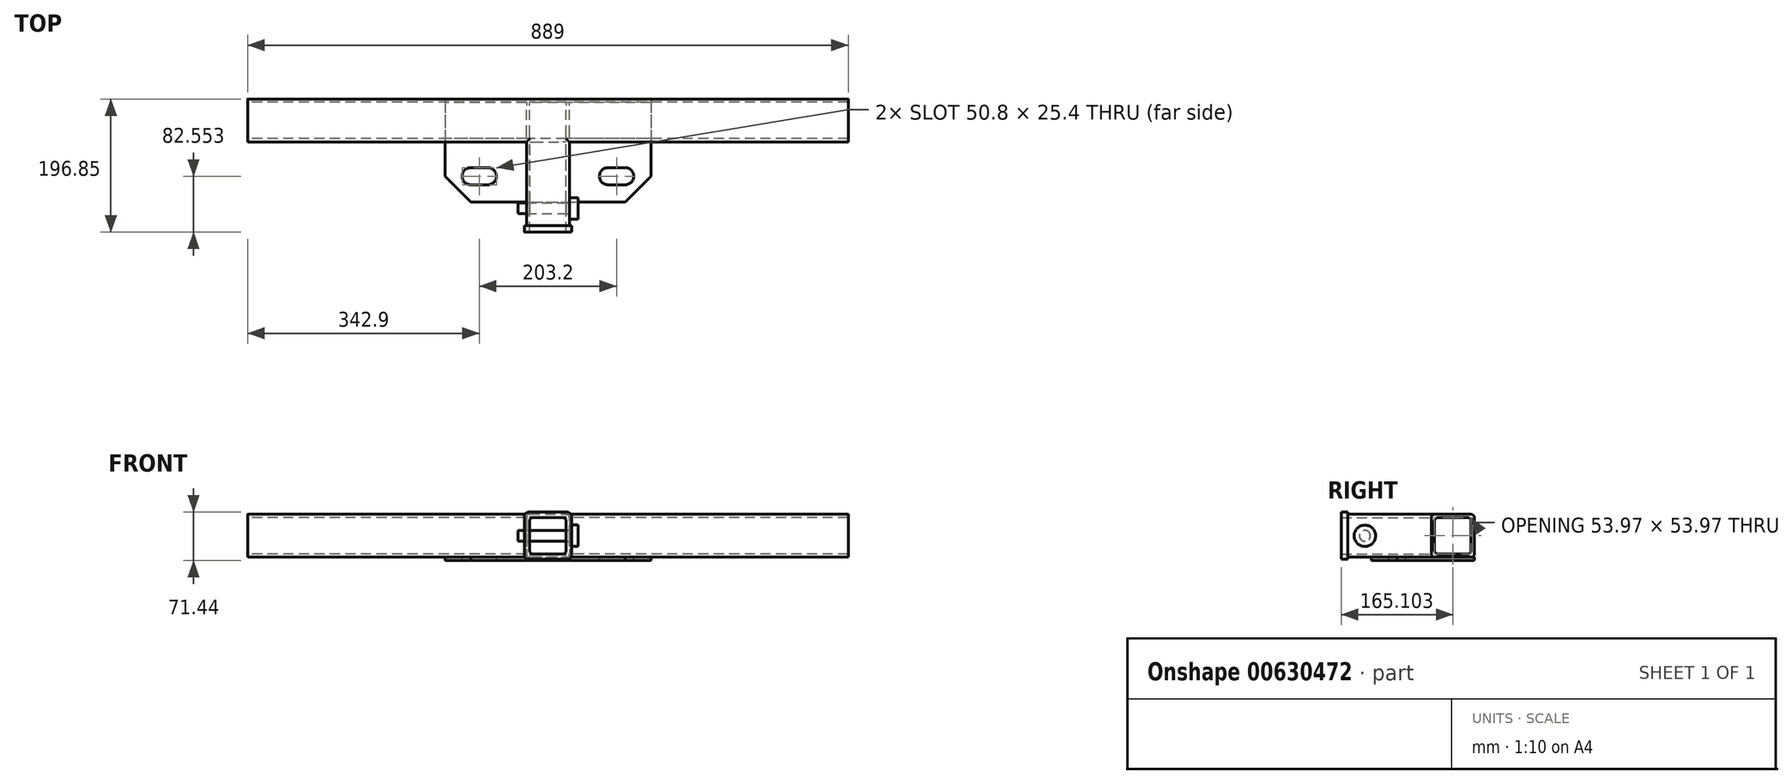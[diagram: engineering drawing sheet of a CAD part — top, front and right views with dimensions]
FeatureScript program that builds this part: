
annotation { "Feature Type Name" : "Feature", "Feature Type Description" : "" }
export const myFeature = defineFeature(function(context is Context, id is Id, definition is map)
    precondition{}
    {
        {
            var Q0;
            Q0=qCreatedBy(makeId("Right.planeOp"),FACE);
            var sketch = newSketch(context, id + "F0", { "sketchPlane" : qUnion([Q0])});
            skLineSegment(sketch, "E0.0", {"start": v(-90.49, 0) * mm, "end": v(-26.99, 0) * mm});
            skLineSegment(sketch, "E0.1", {"start": v(-90.49, 0) * mm, "end": v(-90.49, -63.5) * mm});
            skLineSegment(sketch, "E0.2", {"start": v(-90.49, -63.5) * mm, "end": v(-26.99, -63.5) * mm});
            skLineSegment(sketch, "E0.3", {"start": v(-26.99, 0) * mm, "end": v(-26.99, -63.5) * mm});
            skLineSegment(sketch, "E1.0", {"start": v(-31.75, -4.76) * mm, "end": v(-31.75, -58.74) * mm});
            skLineSegment(sketch, "E1.1", {"start": v(-85.73, -4.76) * mm, "end": v(-31.75, -4.76) * mm});
            skLineSegment(sketch, "E1.2", {"start": v(-85.73, -4.76) * mm, "end": v(-85.73, -58.74) * mm});
            skLineSegment(sketch, "E1.3", {"start": v(-85.73, -58.74) * mm, "end": v(-31.75, -58.74) * mm});
            skSolve(sketch);
        }
        {
            var Q0;
            Q0=makeQuery(id+"F0.imprint","IMPRINT",FACE,{"disambiguationData":[TD([[makeQuery(id+"F0.imprint","IMPRINT",EDGE,{"derivedFrom":sQuery(id+"F0.wireOp",EDGE,"E0.0")}),-1.0]])]});
            var Q1;
            Q1=qConstructionFilter(qBodyType(qCreatedBy(id+"F0",EDGE),BodyType.WIRE),ConstructionObject.NO);
            extrude(context, id + "F1", {"entities" : qUnion([Q0]), "surfaceEntities" : qUnion([Q1]), "depth" : 889 * mm, "symmetric" : true});
        }
        {
            var Q0;
            Q0=makeQuery(id+"F1.opExtrude","SWEPT_FACE",FACE,{"disambiguationData":[OSD([sQuery(id+"F0.wireOp",EDGE,"E0.1")])]});
            var sketch = newSketch(context, id + "F2", { "sketchPlane" : qUnion([Q0])});
            skLineSegment(sketch, "E2.bottom", {"start": v(-31.75, 0) * mm, "end": v(31.75, 0) * mm});
            skLineSegment(sketch, "E2.top", {"start": v(-31.75, -63.5) * mm, "end": v(31.75, -63.5) * mm});
            skLineSegment(sketch, "E2.left", {"start": v(-31.75, 0) * mm, "end": v(-31.75, -63.5) * mm});
            skLineSegment(sketch, "E2.right", {"start": v(31.75, 0) * mm, "end": v(31.75, -63.5) * mm});
            skLineSegment(sketch, "E3.0", {"start": v(-26.99, -4.76) * mm, "end": v(-26.99, -58.74) * mm});
            skLineSegment(sketch, "E3.1", {"start": v(-26.99, -4.76) * mm, "end": v(26.99, -4.76) * mm});
            skLineSegment(sketch, "E3.2", {"start": v(26.99, -4.76) * mm, "end": v(26.99, -58.74) * mm});
            skLineSegment(sketch, "E3.3", {"start": v(-26.99, -58.74) * mm, "end": v(26.99, -58.74) * mm});
            skLineSegment(sketch, "E4", {"start": v(0, 0) * mm, "end": v(0, 11.04) * mm, "construction": true});
            skSolve(sketch);
        }
        {
            var Q0;
            Q0=qSketchRegion(id+"F2",true);
            var Q1;
            Q1=makeQuery(id+"F1.opExtrude","SWEPT_BODY",BODY,{"disambiguationData":[OSD([sQuery(id+"F0.wireOp",EDGE,"E0.0"),sQuery(id+"F0.wireOp",EDGE,"E0.1"),sQuery(id+"F0.wireOp",EDGE,"E0.2"),sQuery(id+"F0.wireOp",EDGE,"E0.3"),sQuery(id+"F0.wireOp",EDGE,"E1.0"),sQuery(id+"F0.wireOp",EDGE,"E1.1"),sQuery(id+"F0.wireOp",EDGE,"E1.2"),sQuery(id+"F0.wireOp",EDGE,"E1.3")])]});
            extrude(context, id + "F3", {"entities" : qUnion([Q0]), "operationType" : NewBodyOperationType.ADD, "depth" : 127 * mm, "hasSecondDirection" : true, "secondDirectionBound" : BoundingType.UP_TO_BODY, "secondDirectionOppositeDirection" : true, "secondDirectionBoundEntityBody" : qUnion([Q1]), "secondDirectionDepth" : 25.4 * mm});
        }
        {
            var Q0;
            Q0=makeQuery(id+"F1.opExtrude","SWEPT_EDGE",EDGE,{"disambiguationData":[OSD([sQuery(id+"F0.wireOp",EDGE,"E0.0"),sQuery(id+"F0.wireOp",EDGE,"E0.1")])]});
            var Q1;
            Q1=makeQuery(id+"F1.opExtrude","SWEPT_EDGE",EDGE,{"disambiguationData":[OSD([sQuery(id+"F0.wireOp",EDGE,"E0.0"),sQuery(id+"F0.wireOp",EDGE,"E0.3")])]});
            var Q2;
            Q2=makeQuery(id+"F1.opExtrude","SWEPT_EDGE",EDGE,{"disambiguationData":[OSD([sQuery(id+"F0.wireOp",EDGE,"E0.2"),sQuery(id+"F0.wireOp",EDGE,"E0.3")])]});
            var Q3;
            Q3=makeQuery(id+"F1.opExtrude","SWEPT_EDGE",EDGE,{"disambiguationData":[OSD([sQuery(id+"F0.wireOp",EDGE,"E0.1"),sQuery(id+"F0.wireOp",EDGE,"E0.2")])]});
            var Q4;
            Q4=makeQuery(id+"F1.opExtrude","SWEPT_EDGE",EDGE,{"disambiguationData":[OSD([sQuery(id+"F0.wireOp",EDGE,"E1.0"),sQuery(id+"F0.wireOp",EDGE,"E1.1")])]});
            var Q5;
            Q5=makeQuery(id+"F1.opExtrude","SWEPT_EDGE",EDGE,{"disambiguationData":[OSD([sQuery(id+"F0.wireOp",EDGE,"E1.1"),sQuery(id+"F0.wireOp",EDGE,"E1.2")])]});
            var Q6;
            Q6=makeQuery(id+"F1.opExtrude","SWEPT_EDGE",EDGE,{"disambiguationData":[OSD([sQuery(id+"F0.wireOp",EDGE,"E1.0"),sQuery(id+"F0.wireOp",EDGE,"E1.3")])]});
            var Q7;
            Q7=makeQuery(id+"F1.opExtrude","SWEPT_EDGE",EDGE,{"disambiguationData":[OSD([sQuery(id+"F0.wireOp",EDGE,"E1.2"),sQuery(id+"F0.wireOp",EDGE,"E1.3")])]});
            var Q8;
            Q8=makeQuery(id+"F3.opExtrude","SWEPT_EDGE",EDGE,{"disambiguationData":[OSD([sQuery(id+"F0.wireOp",EDGE,"E0.0"),sQuery(id+"F0.wireOp",EDGE,"E0.1"),sQuery(id+"F2.wireOp",EDGE,"E2.bottom"),sQuery(id+"F2.wireOp",EDGE,"E2.left")])]});
            var Q9;
            Q9=makeQuery(id+"F3.opExtrude","SWEPT_EDGE",EDGE,{"disambiguationData":[OSD([sQuery(id+"F0.wireOp",EDGE,"E0.0"),sQuery(id+"F0.wireOp",EDGE,"E0.1"),sQuery(id+"F2.wireOp",EDGE,"E2.bottom"),sQuery(id+"F2.wireOp",EDGE,"E2.right")])]});
            var Q10;
            Q10=makeQuery(id+"F3.opExtrude","SWEPT_EDGE",EDGE,{"disambiguationData":[OSD([sQuery(id+"F0.wireOp",EDGE,"E0.1"),sQuery(id+"F0.wireOp",EDGE,"E0.2"),sQuery(id+"F2.wireOp",EDGE,"E2.top"),sQuery(id+"F2.wireOp",EDGE,"E2.right")])]});
            var Q11;
            Q11=makeQuery(id+"F3.opExtrude","SWEPT_EDGE",EDGE,{"disambiguationData":[OSD([sQuery(id+"F0.wireOp",EDGE,"E0.1"),sQuery(id+"F0.wireOp",EDGE,"E0.2"),sQuery(id+"F2.wireOp",EDGE,"E2.top"),sQuery(id+"F2.wireOp",EDGE,"E2.left")])]});
            var Q12;
            {var subQ0=sQuery(id+"F2.wireOp",EDGE,"E3.1");var subQ1=sQuery(id+"F2.wireOp",EDGE,"E3.0");Q12=makeQuery(id+"F3.boolean.opBoolean","SPLIT",EDGE,{"disambiguationData":[TD([makeQuery(id+"F1.opExtrude","SWEPT_FACE",FACE,{"disambiguationData":[OSD([sQuery(id+"F0.wireOp",EDGE,"E0.1")])]})])],"derivedFrom":makeQuery(id+"F3.opExtrude","SWEPT_EDGE",EDGE,{"disambiguationData":[OSD([subQ1,subQ0])]})});}
            var Q13;
            {var subQ0=sQuery(id+"F2.wireOp",EDGE,"E3.2");var subQ1=sQuery(id+"F2.wireOp",EDGE,"E3.1");Q13=makeQuery(id+"F3.boolean.opBoolean","SPLIT",EDGE,{"disambiguationData":[TD([makeQuery(id+"F1.opExtrude","SWEPT_FACE",FACE,{"disambiguationData":[OSD([sQuery(id+"F0.wireOp",EDGE,"E0.1")])]})])],"derivedFrom":makeQuery(id+"F3.opExtrude","SWEPT_EDGE",EDGE,{"disambiguationData":[OSD([subQ1,subQ0])]})});}
            var Q14;
            {var subQ0=sQuery(id+"F2.wireOp",EDGE,"E3.3");var subQ1=sQuery(id+"F2.wireOp",EDGE,"E3.0");Q14=makeQuery(id+"F3.boolean.opBoolean","SPLIT",EDGE,{"disambiguationData":[TD([makeQuery(id+"F1.opExtrude","SWEPT_FACE",FACE,{"disambiguationData":[OSD([sQuery(id+"F0.wireOp",EDGE,"E0.1")])]})])],"derivedFrom":makeQuery(id+"F3.opExtrude","SWEPT_EDGE",EDGE,{"disambiguationData":[OSD([subQ1,subQ0])]})});}
            var Q15;
            {var subQ0=sQuery(id+"F2.wireOp",EDGE,"E3.3");var subQ1=sQuery(id+"F2.wireOp",EDGE,"E3.2");Q15=makeQuery(id+"F3.boolean.opBoolean","SPLIT",EDGE,{"disambiguationData":[TD([makeQuery(id+"F1.opExtrude","SWEPT_FACE",FACE,{"disambiguationData":[OSD([sQuery(id+"F0.wireOp",EDGE,"E0.1")])]})])],"derivedFrom":makeQuery(id+"F3.opExtrude","SWEPT_EDGE",EDGE,{"disambiguationData":[OSD([subQ1,subQ0])]})});}
            fillet(context, id + "F4", {"entities" : qUnion([Q0, Q1, Q2, Q3, Q4, Q5, Q6, Q7, Q8, Q9, Q10, Q11, Q12, Q13, Q14, Q15]), "radius" : 5.08 * mm, "tangentPropagation" : true, "allowEdgeOverflow" : false});
        }
        {
            var Q0;
            Q0=makeQuery(id+"F3.boolean.opBoolean","MERGE",FACE,{"derivedFrom":[makeQuery(id+"F1.opExtrude","SWEPT_FACE",FACE,{"disambiguationData":[OSD([sQuery(id+"F0.wireOp",EDGE,"E0.0")])]}),makeQuery(id+"F3.opExtrude","SWEPT_FACE",FACE,{"disambiguationData":[OSD([sQuery(id+"F2.wireOp",EDGE,"E2.bottom")])]})]});
            var sketch = newSketch(context, id + "F5", { "sketchPlane" : qUnion([Q0])});
            skLineSegment(sketch, "E5.0", {"start": v(-444.5, -26.99) * mm, "end": v(444.5, -26.99) * mm});
            skLineSegment(sketch, "E6", {"start": v(0, -3.11) * mm, "end": v(0, -26.99) * mm, "construction": true});
            skLineSegment(sketch, "E7.0", {"start": v(-31.75, -90.49) * mm, "end": v(-444.5, -90.49) * mm});
            skLineSegment(sketch, "E8.0", {"start": v(444.5, -90.49) * mm, "end": v(31.75, -90.49) * mm});
            skLineSegment(sketch, "E9", {"start": v(-101.6, -26.99) * mm, "end": v(-101.6, -90.49) * mm});
            skLineSegment(sketch, "E10.0", {"start": v(-31.75, -217.49) * mm, "end": v(-31.75, -90.49) * mm});
            skLineSegment(sketch, "E10.1", {"start": v(31.75, -90.49) * mm, "end": v(31.75, -217.49) * mm});
            skLineSegment(sketch, "E11", {"start": v(-101.6, -90.49) * mm, "end": v(-31.75, -160.34) * mm});
            skLineSegment(sketch, "E12", {"start": v(-31.75, -160.34) * mm, "end": v(31.75, -160.34) * mm});
            skLineSegment(sketch, "E13", {"start": v(31.75, -160.34) * mm, "end": v(101.6, -90.49) * mm});
            skLineSegment(sketch, "E14", {"start": v(101.6, -90.49) * mm, "end": v(101.6, -26.99) * mm});
            skSolve(sketch);
        }
        {
            var Q0;
            Q0=makeQuery(id+"F3.boolean.opBoolean","MERGE",FACE,{"derivedFrom":[makeQuery(id+"F1.opExtrude","SWEPT_FACE",FACE,{"disambiguationData":[OSD([sQuery(id+"F0.wireOp",EDGE,"E0.2")])]}),makeQuery(id+"F3.opExtrude","SWEPT_FACE",FACE,{"disambiguationData":[OSD([sQuery(id+"F2.wireOp",EDGE,"E2.top")])]})]});
            var sketch = newSketch(context, id + "F6", { "sketchPlane" : qUnion([Q0])});
            skLineSegment(sketch, "E15.0", {"start": v(444.5, 26.99) * mm, "end": v(-444.5, 26.99) * mm});
            skLineSegment(sketch, "E16.bottom", {"start": v(-152.4, 26.99) * mm, "end": v(152.4, 26.99) * mm});
            skLineSegment(sketch, "E16.top", {"start": v(-114.3, 179.39) * mm, "end": v(114.3, 179.39) * mm});
            skLineSegment(sketch, "E16.right", {"start": v(152.4, 26.99) * mm, "end": v(152.4, 141.29) * mm});
            skLineSegment(sketch, "E17", {"start": v(0, 0) * mm, "end": v(0, 26.99) * mm, "construction": true});
            skLineSegment(sketch, "E18", {"start": v(-152.4, 141.29) * mm, "end": v(-114.3, 179.39) * mm});
            skLineSegment(sketch, "E19", {"start": v(-114.3, 179.39) * mm, "end": v(-152.4, 141.29) * mm});
            skLineSegment(sketch, "E20", {"start": v(152.4, 141.29) * mm, "end": v(114.3, 179.39) * mm});
            skLineSegment(sketch, "E21", {"start": v(-152.4, 26.99) * mm, "end": v(-152.4, 141.29) * mm});
            skLineSegment(sketch, "E22.bottom", {"start": v(-114.3, 153.99) * mm, "end": v(-88.9, 153.99) * mm});
            skLineSegment(sketch, "E22.top", {"start": v(-114.3, 128.59) * mm, "end": v(-88.9, 128.59) * mm});
            skLineSegment(sketch, "E22.left", {"start": v(-127, 141.29) * mm, "end": v(-127, 141.29) * mm});
            skLineSegment(sketch, "E22.right", {"start": v(-76.2, 141.29) * mm, "end": v(-76.2, 141.29) * mm});
            skPoint(sketch, "E23.visualSharp", {"position": v(-127, 153.99) * mm});
            skArc(sketch, "E23.filletArc", {"start": v(-114.3, 153.99) * mm, "mid": v(-123.28, 150.27) * mm, "end": v(-127, 141.29) * mm});
            skPoint(sketch, "E24.visualSharp", {"position": v(-76.2, 153.99) * mm});
            skArc(sketch, "E24.filletArc", {"start": v(-76.2, 141.29) * mm, "mid": v(-79.92, 150.27) * mm, "end": v(-88.9, 153.99) * mm});
            skPoint(sketch, "E25.visualSharp", {"position": v(-76.2, 128.59) * mm});
            skArc(sketch, "E25.filletArc", {"start": v(-88.9, 128.59) * mm, "mid": v(-79.92, 132.3) * mm, "end": v(-76.2, 141.29) * mm});
            skPoint(sketch, "E26.visualSharp", {"position": v(-127, 128.59) * mm});
            skArc(sketch, "E26.filletArc", {"start": v(-127, 141.29) * mm, "mid": v(-123.28, 132.3) * mm, "end": v(-114.3, 128.59) * mm});
            skArc(sketch, "E27.MirrorCS", {"start": v(88.9, 128.59) * mm, "mid": v(79.92, 132.3) * mm, "end": v(76.2, 141.29) * mm});
            skArc(sketch, "E28.MirrorCS", {"start": v(76.2, 141.29) * mm, "mid": v(79.92, 150.27) * mm, "end": v(88.9, 153.99) * mm});
            skArc(sketch, "E29.MirrorCS", {"start": v(127, 141.29) * mm, "mid": v(123.28, 132.3) * mm, "end": v(114.3, 128.59) * mm});
            skArc(sketch, "E30.MirrorCS", {"start": v(114.3, 153.99) * mm, "mid": v(123.28, 150.27) * mm, "end": v(127, 141.29) * mm});
            skLineSegment(sketch, "E31.MirrorCS", {"start": v(127, 141.29) * mm, "end": v(127, 141.29) * mm});
            skLineSegment(sketch, "E32.MirrorCS", {"start": v(76.2, 141.29) * mm, "end": v(76.2, 141.29) * mm});
            skPoint(sketch, "E33.MirrorP", {"position": v(76.2, 153.99) * mm});
            skPoint(sketch, "E34.MirrorP", {"position": v(76.2, 128.59) * mm});
            skLineSegment(sketch, "E35.MirrorCS", {"start": v(114.3, 153.99) * mm, "end": v(88.9, 153.99) * mm});
            skLineSegment(sketch, "E36.MirrorCS", {"start": v(114.3, 128.59) * mm, "end": v(88.9, 128.59) * mm});
            skPoint(sketch, "E37.MirrorP", {"position": v(127, 128.59) * mm});
            skPoint(sketch, "E38.MirrorP", {"position": v(127, 153.99) * mm});
            skSolve(sketch);
        }
        {
            var Q0;
            Q0=qSketchRegion(id+"F6",true);
            extrude(context, id + "F7", {"entities" : qUnion([Q0]), "operationType" : NewBodyOperationType.ADD, "depth" : 4.76 * mm});
        }
        {
            var Q0;
            Q0=makeQuery(id+"F3.opExtrude","CAP_FACE",FACE,{"disambiguationData":[OSD([sQuery(id+"F2.wireOp",EDGE,"E2.bottom"),sQuery(id+"F2.wireOp",EDGE,"E2.top"),sQuery(id+"F2.wireOp",EDGE,"E2.left"),sQuery(id+"F2.wireOp",EDGE,"E2.right"),sQuery(id+"F2.wireOp",EDGE,"E3.0"),sQuery(id+"F2.wireOp",EDGE,"E3.1"),sQuery(id+"F2.wireOp",EDGE,"E3.2"),sQuery(id+"F2.wireOp",EDGE,"E3.3")])],"isStart":false});
            var sketch = newSketch(context, id + "F8", { "sketchPlane" : qUnion([Q0])});
            skLineSegment(sketch, "E39.0", {"start": v(-21.9, -4.76) * mm, "end": v(21.9, -4.76) * mm});
            skArc(sketch, "E39.1", {"start": v(-26.99, -9.84) * mm, "mid": v(-25.5, -6.25) * mm, "end": v(-21.9, -4.76) * mm});
            skLineSegment(sketch, "E39.2", {"start": v(-26.99, -9.84) * mm, "end": v(-26.99, -53.66) * mm});
            skArc(sketch, "E39.3", {"start": v(-21.9, -58.74) * mm, "mid": v(-25.5, -57.25) * mm, "end": v(-26.99, -53.66) * mm});
            skLineSegment(sketch, "E39.4", {"start": v(-21.9, -58.74) * mm, "end": v(21.9, -58.74) * mm});
            skArc(sketch, "E39.5", {"start": v(26.99, -53.66) * mm, "mid": v(25.5, -57.25) * mm, "end": v(21.9, -58.74) * mm});
            skLineSegment(sketch, "E39.6", {"start": v(26.99, -9.84) * mm, "end": v(26.99, -53.66) * mm});
            skArc(sketch, "E39.7", {"start": v(21.9, -4.76) * mm, "mid": v(25.5, -6.25) * mm, "end": v(26.99, -9.84) * mm});
            skLineSegment(sketch, "E40.bottom", {"start": v(-28.58, 3.18) * mm, "end": v(28.58, 3.18) * mm});
            skLineSegment(sketch, "E40.top", {"start": v(-28.58, -66.68) * mm, "end": v(28.58, -66.68) * mm});
            skLineSegment(sketch, "E40.left", {"start": v(-34.93, -3.17) * mm, "end": v(-34.93, -60.33) * mm});
            skLineSegment(sketch, "E40.right", {"start": v(34.93, -3.17) * mm, "end": v(34.93, -60.33) * mm});
            skPoint(sketch, "E41.visualSharp", {"position": v(-34.93, 3.18) * mm});
            skArc(sketch, "E41.filletArc", {"start": v(-28.58, 3.17) * mm, "mid": v(-33.07, 1.32) * mm, "end": v(-34.93, -3.17) * mm});
            skPoint(sketch, "E42.visualSharp", {"position": v(34.93, 3.18) * mm});
            skArc(sketch, "E42.filletArc", {"start": v(34.93, -3.17) * mm, "mid": v(33.07, 1.32) * mm, "end": v(28.58, 3.17) * mm});
            skPoint(sketch, "E43.visualSharp", {"position": v(34.93, -66.68) * mm});
            skArc(sketch, "E43.filletArc", {"start": v(28.58, -66.68) * mm, "mid": v(33.07, -64.82) * mm, "end": v(34.93, -60.33) * mm});
            skPoint(sketch, "E44.visualSharp", {"position": v(-34.93, -66.68) * mm});
            skArc(sketch, "E44.filletArc", {"start": v(-34.93, -60.33) * mm, "mid": v(-33.07, -64.82) * mm, "end": v(-28.58, -66.68) * mm});
            skSolve(sketch);
        }
        {
            var Q0;
            Q0=qSketchRegion(id+"F8",true);
            extrude(context, id + "F9", {"entities" : qUnion([Q0]), "operationType" : NewBodyOperationType.ADD, "depth" : 6.35 * mm, "hasSecondDirection" : true, "secondDirectionOppositeDirection" : true, "secondDirectionDepth" : 3.17 * mm});
        }
        {
            var Q0;
            Q0=makeQuery(id+"F9.opExtrude","CAP_FACE",FACE,{"disambiguationData":[OSD([sQuery(id+"F8.wireOp",EDGE,"E39.0"),sQuery(id+"F8.wireOp",EDGE,"E39.1"),sQuery(id+"F8.wireOp",EDGE,"E39.2"),sQuery(id+"F8.wireOp",EDGE,"E39.3"),sQuery(id+"F8.wireOp",EDGE,"E39.4"),sQuery(id+"F8.wireOp",EDGE,"E39.5"),sQuery(id+"F8.wireOp",EDGE,"E39.6"),sQuery(id+"F8.wireOp",EDGE,"E39.7"),sQuery(id+"F8.wireOp",EDGE,"E40.bottom"),sQuery(id+"F8.wireOp",EDGE,"E40.top"),sQuery(id+"F8.wireOp",EDGE,"E40.left"),sQuery(id+"F8.wireOp",EDGE,"E40.right"),sQuery(id+"F8.wireOp",EDGE,"E41.filletArc"),sQuery(id+"F8.wireOp",EDGE,"E42.filletArc"),sQuery(id+"F8.wireOp",EDGE,"E43.filletArc"),sQuery(id+"F8.wireOp",EDGE,"E44.filletArc")])],"isStart":false});
            var sketch = newSketch(context, id + "F10", { "sketchPlane" : qUnion([Q0])});
            skLineSegment(sketch, "E45.bottom", {"start": v(-19.05, -6.35) * mm, "end": v(19.05, -6.35) * mm});
            skLineSegment(sketch, "E45.top", {"start": v(-19.05, -57.15) * mm, "end": v(19.05, -57.15) * mm});
            skLineSegment(sketch, "E45.left", {"start": v(-25.4, -12.7) * mm, "end": v(-25.4, -50.8) * mm});
            skLineSegment(sketch, "E45.right", {"start": v(25.4, -12.7) * mm, "end": v(25.4, -50.8) * mm});
            skLineSegment(sketch, "E46", {"start": v(0, 0) * mm, "end": v(0, -4.76) * mm, "construction": true});
            skPoint(sketch, "E47.visualSharp", {"position": v(-25.4, -6.35) * mm});
            skArc(sketch, "E47.filletArc", {"start": v(-19.05, -6.35) * mm, "mid": v(-23.54, -8.2) * mm, "end": v(-25.4, -12.7) * mm});
            skPoint(sketch, "E48.visualSharp", {"position": v(25.4, -6.35) * mm});
            skArc(sketch, "E48.filletArc", {"start": v(25.4, -12.7) * mm, "mid": v(23.54, -8.2) * mm, "end": v(19.05, -6.35) * mm});
            skPoint(sketch, "E49.visualSharp", {"position": v(25.4, -57.15) * mm});
            skArc(sketch, "E49.filletArc", {"start": v(19.05, -57.15) * mm, "mid": v(23.54, -55.3) * mm, "end": v(25.4, -50.8) * mm});
            skPoint(sketch, "E50.visualSharp", {"position": v(-25.4, -57.15) * mm});
            skArc(sketch, "E50.filletArc", {"start": v(-25.4, -50.8) * mm, "mid": v(-23.54, -55.3) * mm, "end": v(-19.05, -57.15) * mm});
            skLineSegment(sketch, "E51.bottom", {"start": v(-14.29, -11.11) * mm, "end": v(14.29, -11.11) * mm});
            skLineSegment(sketch, "E51.top", {"start": v(-14.29, -52.39) * mm, "end": v(14.29, -52.39) * mm});
            skLineSegment(sketch, "E51.left", {"start": v(-20.64, -17.46) * mm, "end": v(-20.64, -46.04) * mm});
            skLineSegment(sketch, "E51.right", {"start": v(20.64, -17.46) * mm, "end": v(20.64, -46.04) * mm});
            skPoint(sketch, "E52.visualSharp", {"position": v(-20.64, -11.11) * mm});
            skArc(sketch, "E52.filletArc", {"start": v(-14.29, -11.11) * mm, "mid": v(-18.78, -12.97) * mm, "end": v(-20.64, -17.46) * mm});
            skPoint(sketch, "E53.visualSharp", {"position": v(20.64, -11.11) * mm});
            skArc(sketch, "E53.filletArc", {"start": v(20.64, -17.46) * mm, "mid": v(18.78, -12.97) * mm, "end": v(14.29, -11.11) * mm});
            skPoint(sketch, "E54.visualSharp", {"position": v(-20.64, -52.39) * mm});
            skArc(sketch, "E54.filletArc", {"start": v(-20.64, -46.04) * mm, "mid": v(-18.78, -50.53) * mm, "end": v(-14.29, -52.39) * mm});
            skPoint(sketch, "E55.visualSharp", {"position": v(20.64, -52.39) * mm});
            skArc(sketch, "E55.filletArc", {"start": v(14.29, -52.39) * mm, "mid": v(18.78, -50.53) * mm, "end": v(20.64, -46.04) * mm});
            skSolve(sketch);
        }
        {
            var Q0;
            {var subQ1=sQuery(id+"F2.wireOp",EDGE,"E2.right");Q0=makeQuery(id+"F3.boolean.opBoolean","SPLIT",FACE,{"disambiguationData":[TD([makeQuery(id+"F1.opExtrude","SWEPT_FACE",FACE,{"disambiguationData":[OSD([sQuery(id+"F0.wireOp",EDGE,"E0.0")])]})])],"derivedFrom":makeQuery(id+"F3.opExtrude","SWEPT_FACE",FACE,{"disambiguationData":[OSD([subQ1])]})});}
            var sketch = newSketch(context, id + "F11", { "sketchPlane" : qUnion([Q0])});
            skCircle(sketch, "E56", {"center": v(-188.91, -31.75) * mm, "radius": 8.33 * mm});
            skPoint(sketch, "E57", {"position": v(-214.31, -31.75) * mm});
            skSolve(sketch);
        }
        {
            var Q0;
            Q0=qSketchRegion(id+"F11",true);
            extrude(context, id + "F12", {"entities" : qUnion([Q0]), "operationType" : NewBodyOperationType.REMOVE, "endBound" : BoundingType.THROUGH_ALL, "oppositeDirection" : true, "depth" : 25.4 * mm});
        }
        {
            var Q0;
            {var subQ1=sQuery(id+"F2.wireOp",EDGE,"E2.right");Q0=makeQuery(id+"F3.boolean.opBoolean","SPLIT",FACE,{"disambiguationData":[TD([makeQuery(id+"F1.opExtrude","SWEPT_FACE",FACE,{"disambiguationData":[OSD([sQuery(id+"F0.wireOp",EDGE,"E0.0")])]})])],"derivedFrom":makeQuery(id+"F3.opExtrude","SWEPT_FACE",FACE,{"disambiguationData":[OSD([subQ1])]})});}
            var sketch = newSketch(context, id + "F13", { "sketchPlane" : qUnion([Q0])});
            skCircle(sketch, "E58", {"center": v(-188.91, -31.75) * mm, "radius": 15.88 * mm});
            skSolve(sketch);
        }
        {
            var Q0;
            Q0=qSketchRegion(id+"F13",true);
            extrude(context, id + "F14", {"entities" : qUnion([Q0]), "depth" : 12.7 * mm});
        }
        {
            var Q0;
            Q0=makeQuery(id+"F14.opExtrude","CAP_FACE",FACE,{"disambiguationData":[OSD([sQuery(id+"F13.wireOp",EDGE,"E58")])],"isStart":true});
            var sketch = newSketch(context, id + "F15", { "sketchPlane" : qUnion([Q0])});
            skCircle(sketch, "E59", {"center": v(188.91, -31.75) * mm, "radius": 7.94 * mm});
            skSolve(sketch);
        }
        {
            var Q0;
            Q0=qSketchRegion(id+"F15",true);
            extrude(context, id + "F16", {"entities" : qUnion([Q0]), "operationType" : NewBodyOperationType.ADD, "depth" : 76.2 * mm});
        }
    });
